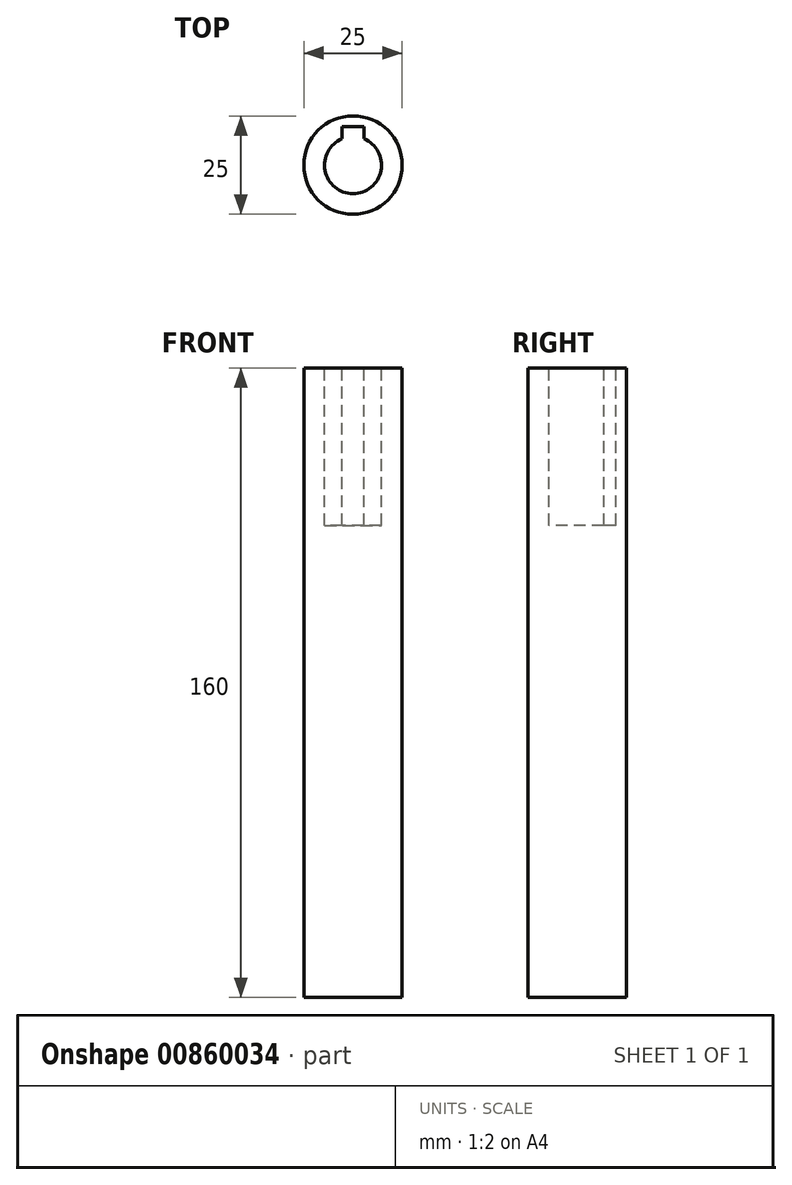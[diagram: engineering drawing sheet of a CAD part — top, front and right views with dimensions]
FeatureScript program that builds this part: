
annotation { "Feature Type Name" : "Feature", "Feature Type Description" : "" }
export const myFeature = defineFeature(function(context is Context, id is Id, definition is map)
    precondition{}
    {
        {
            var Q0;
            Q0=qCreatedBy(makeId("Top.planeOp"),FACE);
            var sketch = newSketch(context, id + "F0", { "sketchPlane" : qUnion([Q0])});
            skCircle(sketch, "E0", {"center": v(0, 0) * mm, "radius": 12.5 * mm});
            skSolve(sketch);
        }
        {
            var Q0;
            Q0=qSketchRegion(id+"F0",true);
            var Q1;
            Q1=qSketchRegion(id+"F2",true);
            extrude(context, id + "F1", {"entities" : qUnion([Q0, Q1]), "depth" : 160 * mm, "offsetDistance" : 25 * mm});
        }
        {
            var Q0;
            Q0=makeQuery(id+"F1.opExtrude","CAP_FACE",FACE,{"disambiguationData":[OSD([sQuery(id+"F0.wireOp",EDGE,"E0")])],"isStart":false});
            var sketch = newSketch(context, id + "F2", { "sketchPlane" : qUnion([Q0])});
            skCircle(sketch, "E1", {"center": v(0, 0) * mm, "radius": 7.25 * mm});
            skLineSegment(sketch, "E2.bottom", {"start": v(2.75, 9.75) * mm, "end": v(-2.75, 9.75) * mm});
            skLineSegment(sketch, "E2.top", {"start": v(2.75, 4.75) * mm, "end": v(-2.75, 4.75) * mm});
            skLineSegment(sketch, "E2.left", {"start": v(2.75, 9.75) * mm, "end": v(2.75, 4.75) * mm});
            skLineSegment(sketch, "E2.right", {"start": v(-2.75, 9.75) * mm, "end": v(-2.75, 4.75) * mm});
            skPoint(sketch, "E2.middle", {"position": v(0, 7.25) * mm});
            skSolve(sketch);
        }
        {
            var Q0;
            Q0=qSketchRegion(id+"F2",true);
            extrude(context, id + "F3", {"entities" : qUnion([Q0]), "operationType" : NewBodyOperationType.REMOVE, "oppositeDirection" : true, "depth" : 40 * mm, "offsetDistance" : 25 * mm});
        }
    });
